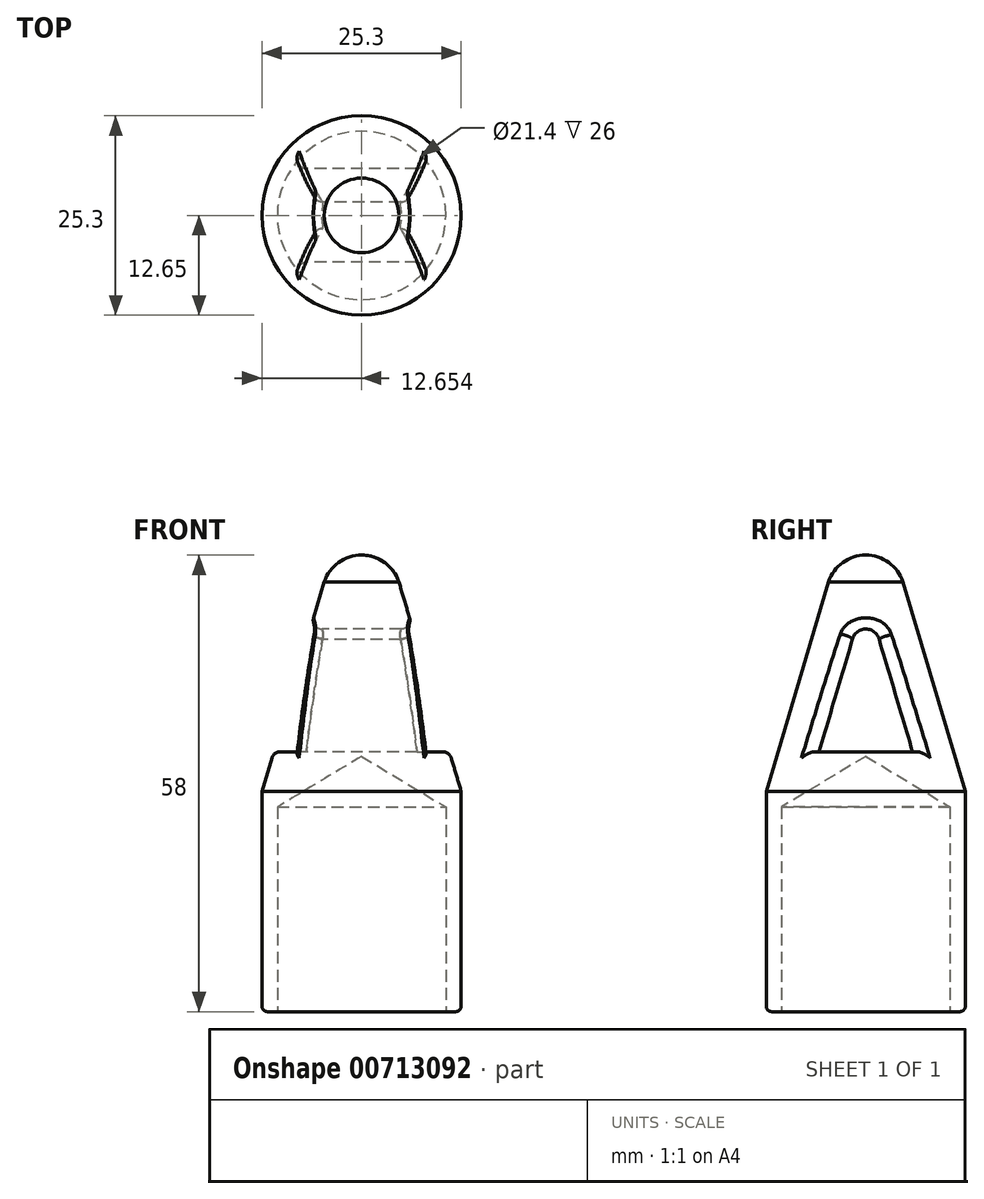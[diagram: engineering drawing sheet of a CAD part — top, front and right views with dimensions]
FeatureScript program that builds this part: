
annotation { "Feature Type Name" : "Feature", "Feature Type Description" : "" }
export const myFeature = defineFeature(function(context is Context, id is Id, definition is map)
    precondition{}
    {
        {
            var Q0;
            Q0=qCreatedBy(makeId("Front.planeOp"),FACE);
            var sketch = newSketch(context, id + "F0", { "sketchPlane" : qUnion([Q0])});
            skLineSegment(sketch, "E0.bottom", {"start": v(0.3, -10.32) * mm, "end": v(12.95, -10.32) * mm});
            skLineSegment(sketch, "E0.top", {"start": v(0.3, -38.32) * mm, "end": v(12.95, -38.32) * mm});
            skLineSegment(sketch, "E0.left", {"start": v(0.3, -10.32) * mm, "end": v(0.3, -38.32) * mm});
            skArc(sketch, "E1", {"start": v(12.95, 19.68) * mm, "mid": v(10.03, 18.74) * mm, "end": v(8.21, 16.27) * mm});
            skPoint(sketch, "E1.centerSnap0", {"position": v(12.95, -10.32) * mm});
            skLineSegment(sketch, "E2", {"start": v(0.3, -10.32) * mm, "end": v(8.21, 16.27) * mm});
            skPoint(sketch, "E0.right.start.orphan", {"position": v(25.6, -10.32) * mm});
            skLineSegment(sketch, "E3", {"start": v(12.95, 19.68) * mm, "end": v(12.95, -38.32) * mm});
            skPoint(sketch, "E4.start.orphan", {"position": v(12.95, 28.1) * mm});
            skSolve(sketch);
        }
        {
            var Q0;
            {var subQ0=sQuery(id+"F0.wireOp",EDGE,"E0.bottom");Q0=makeQuery(id+"F0.imprint","IMPRINT",FACE,{"disambiguationData":[TD([[makeQuery(id+"F0.imprint","IMPRINT",EDGE,{"derivedFrom":subQ0}),1.0]])]});}
            var Q1;
            {var subQ0=sQuery(id+"F0.wireOp",EDGE,"E0.bottom");Q1=makeQuery(id+"F0.imprint","IMPRINT",FACE,{"disambiguationData":[TD([[makeQuery(id+"F0.imprint","IMPRINT",EDGE,{"derivedFrom":subQ0}),-1.0]])]});}
            var Q2;
            Q2=sQuery(id+"F0.wireOp",EDGE,"E3");
            revolve(context, id + "F1", {"surfaceOperationType" : NewSurfaceOperationType.NEW, "entities" : qUnion([Q0, Q1]), "axis" : qUnion([Q2]), "revolveType" : RevolveType.FULL});
        }
        {
            var Q0;
            Q0=makeQuery(id+"F1.opRevolve","SWEPT_FACE",FACE,{"disambiguationData":[OSD([sQuery(id+"F0.wireOp",EDGE,"E0.top")])]});
            var sketch = newSketch(context, id + "F2", { "sketchPlane" : qUnion([Q0])});
            skPoint(sketch, "E5", {"position": v(12.95, 0) * mm});
            skSolve(sketch);
        }
        {
            var Q0;
            Q0=sQuery(id+"F2.wireOp",VERTEX,"E5");
            var Q1;
            Q1=makeQuery(id+"F1.opRevolve","SWEPT_BODY",BODY,{"disambiguationData":[OSD([sQuery(id+"F0.wireOp",EDGE,"E0.top"),sQuery(id+"F0.wireOp",EDGE,"E0.left"),sQuery(id+"F0.wireOp",EDGE,"E1"),sQuery(id+"F0.wireOp",EDGE,"E2"),sQuery(id+"F0.wireOp",EDGE,"E3")])]});
            hole(context, id + "F3", {"style" : HoleStyle.SIMPLE, "endStyle" : HoleEndStyle.BLIND, "holeDiameter" : 21.4 * mm, "majorDiameter" : 5 * mm, "holeDepth" : 26 * mm, "isTappedThrough" : true, "tappedDepth" : 12 * mm, "tapClearance" : 3, "startFromSketch" : true, "locations" : qUnion([Q0]), "scope" : qUnion([Q1])});
        }
        {
            var Q0;
            Q0=qCreatedBy(makeId("Right.planeOp"),FACE);
            var sketch = newSketch(context, id + "F4", { "sketchPlane" : qUnion([Q0])});
            skLineSegment(sketch, "E6.0", {"start": v(1.65, 9.14) * mm, "end": v(5.95, -5.32) * mm});
            skLineSegment(sketch, "E6.1", {"start": v(-5.95, -5.32) * mm, "end": v(-1.67, 9.06) * mm});
            skLineSegment(sketch, "E6.2", {"start": v(-5.95, -5.32) * mm, "end": v(5.95, -5.32) * mm});
            skPoint(sketch, "E7.first.point", {"position": v(-1.67, 9.06) * mm});
            skPoint(sketch, "E7.second.point", {"position": v(1.7, 8.96) * mm});
            skArc(sketch, "E8", {"start": v(1.7, 8.96) * mm, "mid": v(0.04, 10.3) * mm, "end": v(-1.68, 9.03) * mm});
            skPoint(sketch, "E8.third.point", {"position": v(0, 10.3) * mm});
            skSolve(sketch);
        }
        {
            var Q0;
            Q0=qSketchRegion(id+"F4",true);
            extrude(context, id + "F5", {"entities" : qUnion([Q0]), "operationType" : NewBodyOperationType.REMOVE, "depth" : 25 * mm, "offsetDistance" : 25 * mm});
        }
        {
            var Q0;
            Q0=makeQuery(id+"F5.boolean.opBoolean","INTERSECT",EDGE,{"disambiguationData":[OD(0.0)],"derivedFrom":[makeQuery(id+"F1.opRevolve","SWEPT_FACE",FACE,{"disambiguationData":[OSD([sQuery(id+"F0.wireOp",EDGE,"E2")])]}),makeQuery(id+"F5.opExtrude","SWEPT_FACE",FACE,{"disambiguationData":[OSD([sQuery(id+"F4.wireOp",EDGE,"E6.0")])]})]});
            var Q1;
            Q1=makeQuery(id+"F5.boolean.opBoolean","INTERSECT",EDGE,{"disambiguationData":[OD(0.0)],"derivedFrom":[makeQuery(id+"F1.opRevolve","SWEPT_FACE",FACE,{"disambiguationData":[OSD([sQuery(id+"F0.wireOp",EDGE,"E2")])]}),makeQuery(id+"F5.opExtrude","SWEPT_FACE",FACE,{"disambiguationData":[OSD([sQuery(id+"F4.wireOp",EDGE,"E6.1")])]})]});
            var Q2;
            Q2=makeQuery(id+"F5.boolean.opBoolean","INTERSECT",EDGE,{"disambiguationData":[OD(0.0)],"derivedFrom":[makeQuery(id+"F1.opRevolve","SWEPT_FACE",FACE,{"disambiguationData":[OSD([sQuery(id+"F0.wireOp",EDGE,"E2")])]}),makeQuery(id+"F5.opExtrude","SWEPT_FACE",FACE,{"disambiguationData":[OSD([sQuery(id+"F4.wireOp",EDGE,"E6.2")])]})]});
            var Q3;
            Q3=makeQuery(id+"F5.boolean.opBoolean","INTERSECT",EDGE,{"disambiguationData":[OD(0.0)],"derivedFrom":[makeQuery(id+"F1.opRevolve","SWEPT_FACE",FACE,{"disambiguationData":[OSD([sQuery(id+"F0.wireOp",EDGE,"E2")])]}),makeQuery(id+"F5.opExtrude","SWEPT_FACE",FACE,{"disambiguationData":[OSD([sQuery(id+"F4.wireOp",EDGE,"E8")])]})]});
            var Q4;
            Q4=makeQuery(id+"F5.boolean.opBoolean","INTERSECT",EDGE,{"disambiguationData":[OD(1.0)],"derivedFrom":[makeQuery(id+"F1.opRevolve","SWEPT_FACE",FACE,{"disambiguationData":[OSD([sQuery(id+"F0.wireOp",EDGE,"E2")])]}),makeQuery(id+"F5.opExtrude","SWEPT_FACE",FACE,{"disambiguationData":[OSD([sQuery(id+"F4.wireOp",EDGE,"E6.1")])]})]});
            var Q5;
            Q5=makeQuery(id+"F5.boolean.opBoolean","INTERSECT",EDGE,{"disambiguationData":[OD(1.0)],"derivedFrom":[makeQuery(id+"F1.opRevolve","SWEPT_FACE",FACE,{"disambiguationData":[OSD([sQuery(id+"F0.wireOp",EDGE,"E2")])]}),makeQuery(id+"F5.opExtrude","SWEPT_FACE",FACE,{"disambiguationData":[OSD([sQuery(id+"F4.wireOp",EDGE,"E6.2")])]})]});
            var Q6;
            Q6=makeQuery(id+"F5.boolean.opBoolean","INTERSECT",EDGE,{"disambiguationData":[OD(1.0)],"derivedFrom":[makeQuery(id+"F1.opRevolve","SWEPT_FACE",FACE,{"disambiguationData":[OSD([sQuery(id+"F0.wireOp",EDGE,"E2")])]}),makeQuery(id+"F5.opExtrude","SWEPT_FACE",FACE,{"disambiguationData":[OSD([sQuery(id+"F4.wireOp",EDGE,"E6.0")])]})]});
            var Q7;
            Q7=makeQuery(id+"F5.boolean.opBoolean","INTERSECT",EDGE,{"disambiguationData":[OD(1.0)],"derivedFrom":[makeQuery(id+"F1.opRevolve","SWEPT_FACE",FACE,{"disambiguationData":[OSD([sQuery(id+"F0.wireOp",EDGE,"E2")])]}),makeQuery(id+"F5.opExtrude","SWEPT_FACE",FACE,{"disambiguationData":[OSD([sQuery(id+"F4.wireOp",EDGE,"E8")])]})]});
            fillet(context, id + "F6", {"entities" : qUnion([Q0, Q1, Q2, Q3, Q4, Q5, Q6, Q7]), "radius" : 1.1 * mm, "tangentPropagation" : true, "allowEdgeOverflow" : false});
        }
        {
            var Q0;
            Q0=makeQuery(id+"F1.opRevolve","SWEPT_EDGE",EDGE,{"disambiguationData":[OSD([sQuery(id+"F0.wireOp",EDGE,"E0.top"),sQuery(id+"F0.wireOp",EDGE,"E0.left")])]});
            fillet(context, id + "F7", {"entities" : qUnion([Q0]), "radius" : 0.7 * mm, "tangentPropagation" : true, "allowEdgeOverflow" : false});
        }
    });
